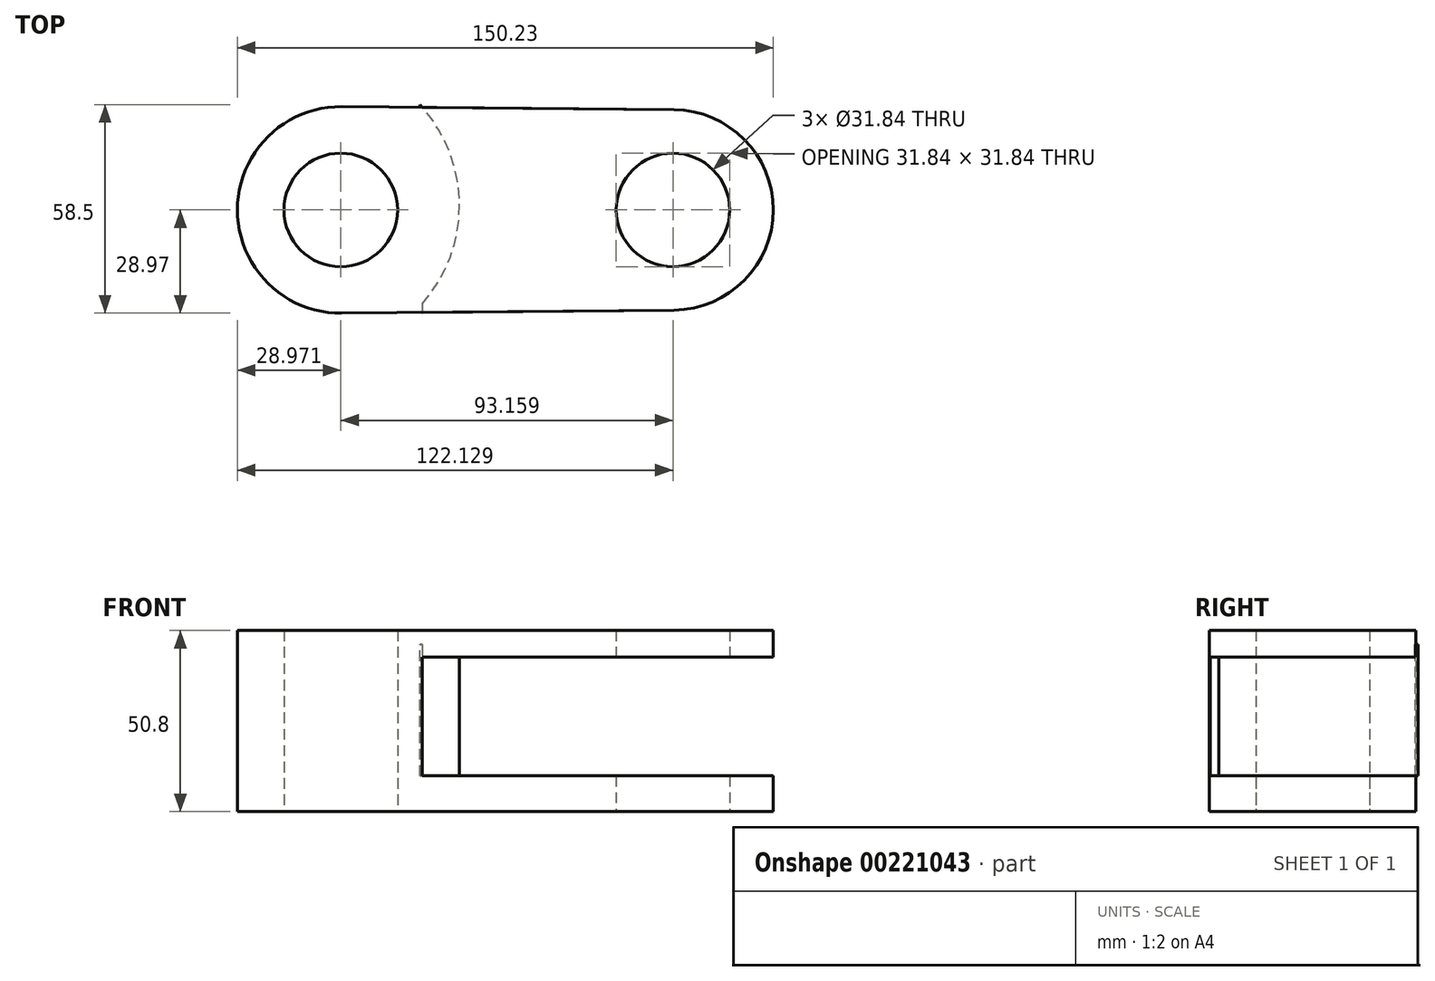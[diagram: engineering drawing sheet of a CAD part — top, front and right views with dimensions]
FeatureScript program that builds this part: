
annotation { "Feature Type Name" : "Feature", "Feature Type Description" : "" }
export const myFeature = defineFeature(function(context is Context, id is Id, definition is map)
    precondition{}
    {
        {
            var Q0;
            Q0=qCreatedBy(makeId("Top.planeOp"),FACE);
            var sketch = newSketch(context, id + "F0", { "sketchPlane" : qUnion([Q0])});
            skCircle(sketch, "E0", {"center": v(-46.58, 0) * mm, "radius": 15.92 * mm});
            skCircle(sketch, "E1", {"center": v(46.58, 0) * mm, "radius": 15.92 * mm});
            skArc(sketch, "E2", {"start": v(-46.3, 28.97) * mm, "mid": v(-75.55, 0) * mm, "end": v(-46.3, -28.97) * mm});
            skArc(sketch, "E3", {"start": v(46.84, -28.1) * mm, "mid": v(74.68, 0) * mm, "end": v(46.84, 28.1) * mm});
            skLineSegment(sketch, "E4", {"start": v(-46.3, 28.97) * mm, "end": v(46.84, 28.1) * mm});
            skLineSegment(sketch, "E5", {"start": v(46.84, -28.1) * mm, "end": v(-46.3, -28.97) * mm});
            skArc(sketch, "E6", {"start": v(-46.3, -28.97) * mm, "mid": v(-17.6, 0) * mm, "end": v(-46.3, 28.97) * mm});
            skSolve(sketch);
        }
        {
            var Q0;
            Q0=makeQuery(id+"F0.imprint","IMPRINT",FACE,{"disambiguationData":[TD([[makeQuery(id+"F0.imprint","IMPRINT",EDGE,{"derivedFrom":sQuery(id+"F0.wireOp",EDGE,"E0")}),-1.0]])]});
            extrude(context, id + "F1", {"entities" : qUnion([Q0]), "depth" : 50.8 * mm});
        }
        {
            var Q0;
            Q0=makeQuery(id+"F0.imprint","IMPRINT",FACE,{"disambiguationData":[TD([[makeQuery(id+"F0.imprint","IMPRINT",EDGE,{"derivedFrom":sQuery(id+"F0.wireOp",EDGE,"E1")}),-1.0]])]});
            extrude(context, id + "F2", {"entities" : qUnion([Q0]), "operationType" : NewBodyOperationType.ADD, "depth" : 50.8 * mm});
        }
        {
            var Q0;
            Q0=makeQuery(id+"F2.opExtrude","SWEPT_FACE",FACE,{"disambiguationData":[OSD([sQuery(id+"F0.wireOp",EDGE,"E5")])]});
            var sketch = newSketch(context, id + "F3", { "sketchPlane" : qUnion([Q0])});
            skLineSegment(sketch, "E7.bottom", {"start": v(-24, 43.29) * mm, "end": v(76.2, 43.29) * mm});
            skLineSegment(sketch, "E7.top", {"start": v(-24, 10.01) * mm, "end": v(76.2, 10.01) * mm});
            skLineSegment(sketch, "E7.left", {"start": v(-24, 43.29) * mm, "end": v(-24, 10.01) * mm});
            skLineSegment(sketch, "E7.right", {"start": v(76.2, 43.29) * mm, "end": v(76.2, 10.01) * mm});
            skSolve(sketch);
        }
        {
            var Q0;
            Q0 = qSketchRegion(id + "F3", true);
            extrude(context, id + "F4", {"entities" : qUnion([Q0]), "operationType" : NewBodyOperationType.REMOVE, "oppositeDirection" : true, "depth" : 77.72 * mm});
        }
        {
            var Q0;
            Q0=makeQuery(id+"F4.boolean.opBoolean","COPY",FACE,{"derivedFrom":makeQuery(id+"F4.opExtrude","SWEPT_FACE",FACE,{"disambiguationData":[OSD([sQuery(id+"F3.wireOp",EDGE,"E7.top")])]})});
            var sketch = newSketch(context, id + "F5", { "sketchPlane" : qUnion([Q0])});
            skArc(sketch, "E8", {"start": v(-23.74, -28.76) * mm, "mid": v(-12.63, 0.1) * mm, "end": v(-24.28, 28.77) * mm});
            skSolve(sketch);
        }
        {
            var Q0;
            Q0=makeQuery(id+"F5.imprint","IMPRINT",FACE,{"disambiguationData":[TD([[makeQuery(id+"F5.imprint","IMPRINT",EDGE,{"derivedFrom":sQuery(id+"F5.wireOp",EDGE,"E8")}),-1.0]])]});
            var sketch = newSketch(context, id + "F6", { "sketchPlane" : qUnion([Q0])});
            skLineSegment(sketch, "E9", {"start": v(-24.38, -27.03) * mm, "end": v(-24.38, 29.53) * mm});
            skArc(sketch, "E10", {"start": v(-24.38, -27.03) * mm, "mid": v(-13.28, 1.25) * mm, "end": v(-24.38, 29.53) * mm});
            skSolve(sketch);
        }
        {
            var Q0;
            Q0 = qSketchRegion(id + "F6", true);
            extrude(context, id + "F7", {"entities" : qUnion([Q0]), "operationType" : NewBodyOperationType.ADD, "depth" : 36.83 * mm});
        }
    });
